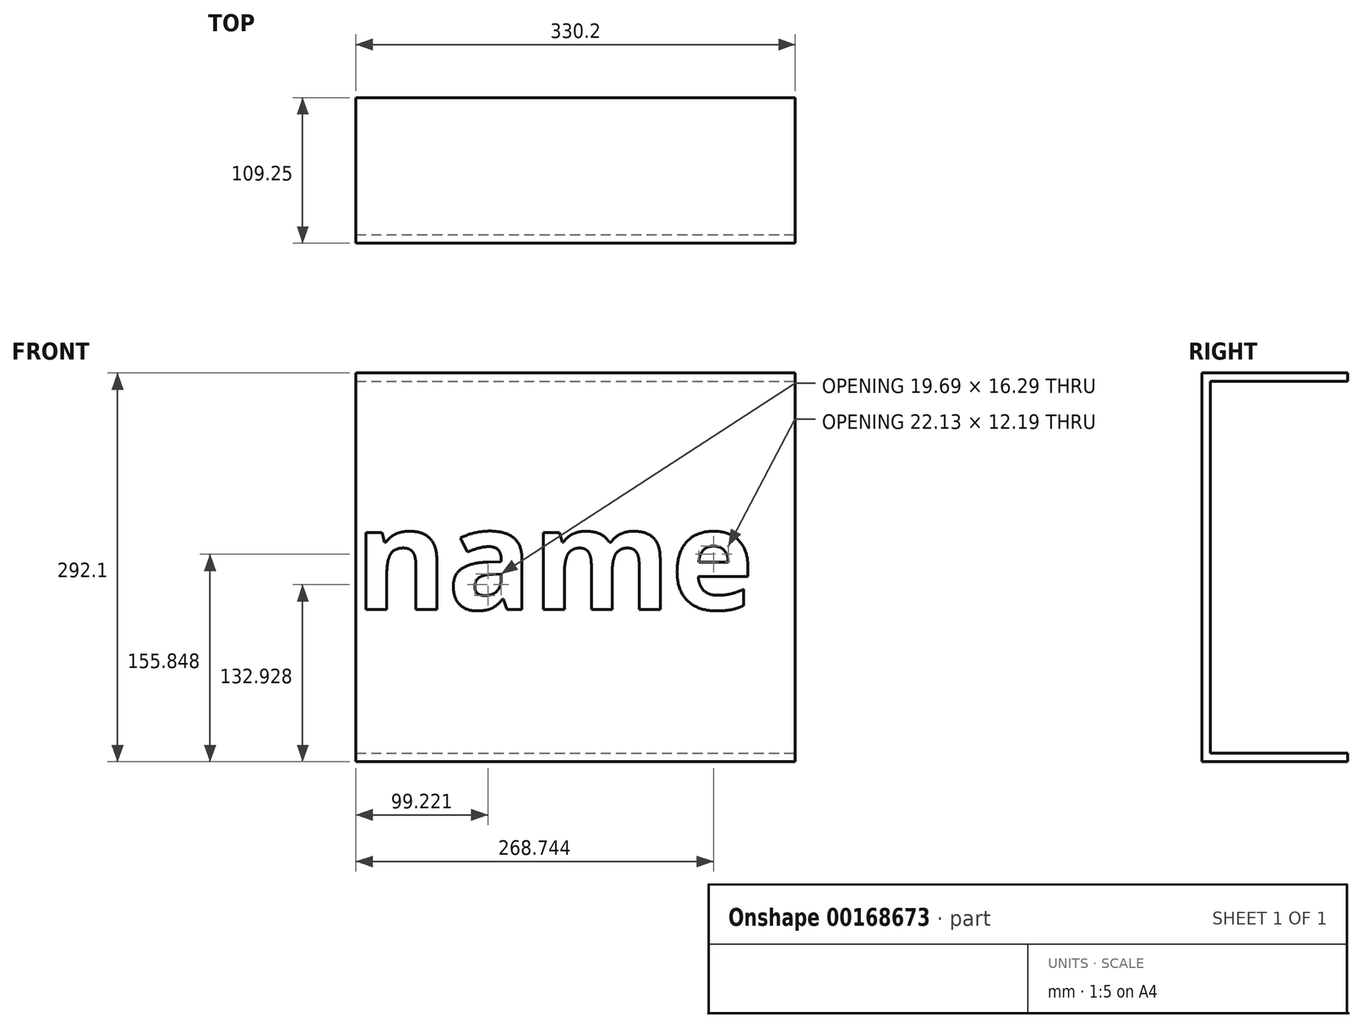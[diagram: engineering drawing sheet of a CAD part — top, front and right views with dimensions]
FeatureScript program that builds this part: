
annotation { "Feature Type Name" : "Feature", "Feature Type Description" : "" }
export const myFeature = defineFeature(function(context is Context, id is Id, definition is map)
    precondition{}
    {
        {
            var Q0;
            Q0=qCreatedBy(makeId("Front.planeOp"),FACE);
            var sketch = newSketch(context, id + "F0", { "sketchPlane" : qUnion([Q0])});
            skLineSegment(sketch, "E0.bottom", {"start": v(-179.35, 211.82) * mm, "end": v(150.85, 211.82) * mm});
            skLineSegment(sketch, "E0.top", {"start": v(-179.35, -80.28) * mm, "end": v(150.85, -80.28) * mm});
            skLineSegment(sketch, "E0.left", {"start": v(-179.35, 211.82) * mm, "end": v(-179.35, -80.28) * mm});
            skLineSegment(sketch, "E0.right", {"start": v(150.85, 211.82) * mm, "end": v(150.85, -80.28) * mm});
            skSolve(sketch);
        }
        {
            var Q0;
            Q0=qSketchRegion(id+"F0",true);
            extrude(context, id + "F1", {"entities" : qUnion([Q0]), "depth" : 109.22 * mm});
        }
        {
            var Q0;
            Q0=makeQuery(id+"F1.opExtrude","CAP_FACE",FACE,{"disambiguationData":[OSD([sQuery(id+"F0.wireOp",EDGE,"E0.bottom"),sQuery(id+"F0.wireOp",EDGE,"E0.top"),sQuery(id+"F0.wireOp",EDGE,"E0.left"),sQuery(id+"F0.wireOp",EDGE,"E0.right")])],"isStart":true});
            var Q1;
            Q1=makeQuery(id+"F1.opExtrude","SWEPT_FACE",FACE,{"disambiguationData":[OSD([sQuery(id+"F0.wireOp",EDGE,"E0.left")])]});
            var Q2;
            Q2=makeQuery(id+"F1.opExtrude","SWEPT_FACE",FACE,{"disambiguationData":[OSD([sQuery(id+"F0.wireOp",EDGE,"E0.right")])]});
            shell(context, id + "F2", {"entities" : qUnion([Q0, Q1, Q2]), "thickness" : 6.35 * mm});
        }
        {
            var Q0;
            Q0=makeQuery(id+"F1.opExtrude","CAP_FACE",FACE,{"disambiguationData":[OSD([sQuery(id+"F0.wireOp",EDGE,"E0.bottom"),sQuery(id+"F0.wireOp",EDGE,"E0.top"),sQuery(id+"F0.wireOp",EDGE,"E0.left"),sQuery(id+"F0.wireOp",EDGE,"E0.right")])],"isStart":false});
            cPlane(context, id + "F3", {"entities" : qUnion([Q0]), "cplaneType" : CPlaneType.OFFSET, "offset" : 0 * mm, "width" : 152.4 * mm, "height" : 152.4 * mm});
        }
        {
            var Q0;
            Q0=qCreatedBy(id+"F3.planeOp",FACE);
            var sketch = newSketch(context, id + "F4", { "sketchPlane" : qUnion([Q0])});
            skText(sketch, "E1", { "text": "name", "fontName": "OpenSans-Bold.ttf"});
            const initialGuessF4  = {"E1": [-0.18015, 0.03402, 1, 0, 0.0762]};
            skSetInitialGuess(sketch, initialGuessF4);
            skSolve(sketch);
        }
        {
            var Q0;
            Q0=qSketchRegion(id+"F4",true);
            extrude(context, id + "F5", {"entities" : qUnion([Q0]), "depth" : 0.03 * mm});
        }
    });
